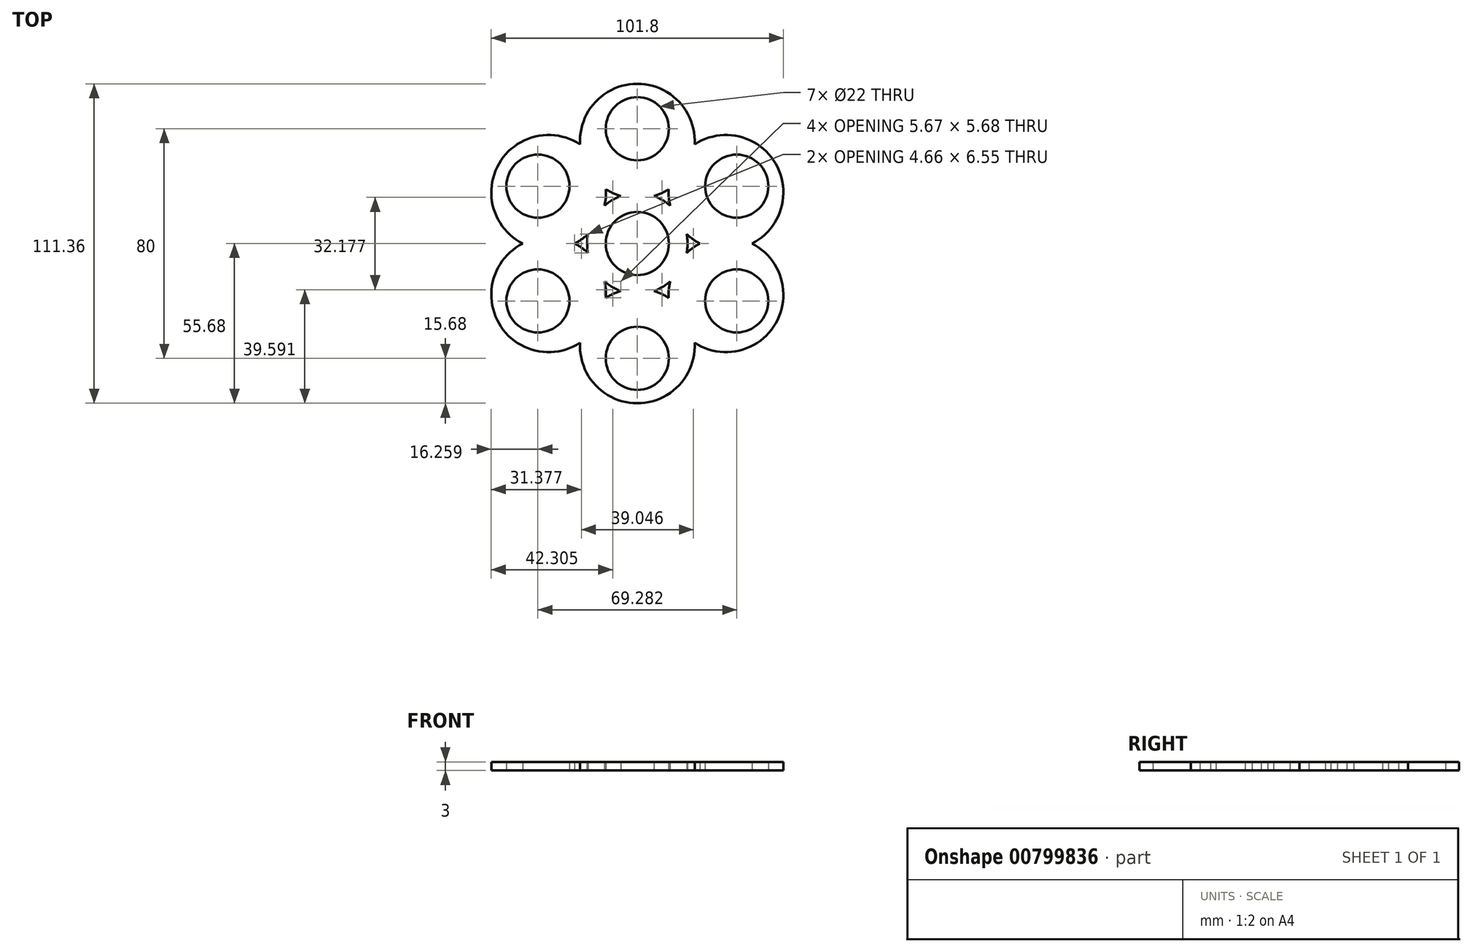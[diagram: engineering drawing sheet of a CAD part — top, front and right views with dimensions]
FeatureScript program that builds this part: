
annotation { "Feature Type Name" : "Feature", "Feature Type Description" : "" }
export const myFeature = defineFeature(function(context is Context, id is Id, definition is map)
    precondition{}
    {
        {
            var Q0;
            Q0=qCreatedBy(makeId("Top.planeOp"),FACE);
            var sketch = newSketch(context, id + "F0", { "sketchPlane" : qUnion([Q0])});
            skArc(sketch, "E0", {"start": v(5.5, 9.53) * mm, "mid": v(0, 11) * mm, "end": v(-5.5, 9.53) * mm});
            skArc(sketch, "E1", {"start": v(-5.76, 16.53) * mm, "mid": v(-7.29, 15.91) * mm, "end": v(-8.75, 15.16) * mm});
            skCircle(sketch, "E2", {"center": v(0, 40) * mm, "radius": 11 * mm});
            skArc(sketch, "E3", {"start": v(-10.93, 18.93) * mm, "mid": v(-8.43, 17.54) * mm, "end": v(-5.76, 16.53) * mm});
            skArc(sketch, "E4.trimOffspring", {"start": v(5.76, 16.53) * mm, "mid": v(8.43, 17.54) * mm, "end": v(10.93, 18.93) * mm});
            skArc(sketch, "E5.trimOffspring", {"start": v(19.97, 34.59) * mm, "mid": v(0, 55.68) * mm, "end": v(-19.97, 34.59) * mm});
            skArc(sketch, "E6.trimOffspring", {"start": v(8.75, 15.16) * mm, "mid": v(7.29, 15.91) * mm, "end": v(5.76, 16.53) * mm});
            skCircle(sketch, "E7.1.0", {"center": v(-34.64, 20) * mm, "radius": 11 * mm});
            skArc(sketch, "E7.1.1", {"start": v(-19.97, 34.59) * mm, "mid": v(-48.22, 27.84) * mm, "end": v(-39.94, 0) * mm});
            skArc(sketch, "E7.1.2", {"start": v(-5.5, 9.53) * mm, "mid": v(-9.53, 5.5) * mm, "end": v(-11, 0) * mm});
            skArc(sketch, "E7.1.3", {"start": v(-11.43, 13.25) * mm, "mid": v(-10.98, 16.07) * mm, "end": v(-10.93, 18.93) * mm});
            skArc(sketch, "E7.1.4", {"start": v(-21.86, 0) * mm, "mid": v(-19.4, 1.47) * mm, "end": v(-17.2, 3.27) * mm});
            skArc(sketch, "E7.1.5", {"start": v(-17.2, 3.27) * mm, "mid": v(-17.42, 1.64) * mm, "end": v(-17.5, 0) * mm});
            skArc(sketch, "E7.1.6", {"start": v(-8.75, 15.16) * mm, "mid": v(-10.14, 14.27) * mm, "end": v(-11.43, 13.25) * mm});
            skCircle(sketch, "E7.2.0", {"center": v(-34.64, -20) * mm, "radius": 11 * mm});
            skArc(sketch, "E7.2.1", {"start": v(-39.94, 0) * mm, "mid": v(-48.22, -27.84) * mm, "end": v(-19.97, -34.59) * mm});
            skArc(sketch, "E7.2.2", {"start": v(-11, 0) * mm, "mid": v(-9.53, -5.5) * mm, "end": v(-5.5, -9.53) * mm});
            skArc(sketch, "E7.2.3", {"start": v(-17.2, -3.27) * mm, "mid": v(-19.4, -1.47) * mm, "end": v(-21.86, 0) * mm});
            skArc(sketch, "E7.2.4", {"start": v(-10.93, -18.93) * mm, "mid": v(-10.98, -16.07) * mm, "end": v(-11.43, -13.25) * mm});
            skArc(sketch, "E7.2.5", {"start": v(-11.43, -13.25) * mm, "mid": v(-10.14, -14.27) * mm, "end": v(-8.75, -15.16) * mm});
            skArc(sketch, "E7.2.6", {"start": v(-17.5, 0) * mm, "mid": v(-17.42, -1.64) * mm, "end": v(-17.2, -3.27) * mm});
            skCircle(sketch, "E7.3.0", {"center": v(0, -40) * mm, "radius": 11 * mm});
            skArc(sketch, "E7.3.1", {"start": v(-19.97, -34.59) * mm, "mid": v(0, -55.68) * mm, "end": v(19.97, -34.59) * mm});
            skArc(sketch, "E7.3.2", {"start": v(-5.5, -9.53) * mm, "mid": v(0, -11) * mm, "end": v(5.5, -9.53) * mm});
            skArc(sketch, "E7.3.3", {"start": v(-5.76, -16.53) * mm, "mid": v(-8.43, -17.54) * mm, "end": v(-10.93, -18.93) * mm});
            skArc(sketch, "E7.3.4", {"start": v(10.93, -18.93) * mm, "mid": v(8.43, -17.54) * mm, "end": v(5.76, -16.53) * mm});
            skArc(sketch, "E7.3.5", {"start": v(5.76, -16.53) * mm, "mid": v(7.29, -15.91) * mm, "end": v(8.75, -15.16) * mm});
            skArc(sketch, "E7.3.6", {"start": v(-8.75, -15.16) * mm, "mid": v(-7.29, -15.91) * mm, "end": v(-5.76, -16.53) * mm});
            skCircle(sketch, "E7.4.0", {"center": v(34.64, -20) * mm, "radius": 11 * mm});
            skArc(sketch, "E7.4.1", {"start": v(19.97, -34.59) * mm, "mid": v(48.22, -27.84) * mm, "end": v(39.94, 0) * mm});
            skArc(sketch, "E7.4.2", {"start": v(5.5, -9.53) * mm, "mid": v(9.53, -5.5) * mm, "end": v(11, 0) * mm});
            skArc(sketch, "E7.4.3", {"start": v(11.43, -13.25) * mm, "mid": v(10.98, -16.07) * mm, "end": v(10.93, -18.93) * mm});
            skArc(sketch, "E7.4.4", {"start": v(21.86, 0) * mm, "mid": v(19.4, -1.47) * mm, "end": v(17.2, -3.27) * mm});
            skArc(sketch, "E7.4.5", {"start": v(17.2, -3.27) * mm, "mid": v(17.42, -1.64) * mm, "end": v(17.5, 0) * mm});
            skArc(sketch, "E7.4.6", {"start": v(8.75, -15.16) * mm, "mid": v(10.14, -14.27) * mm, "end": v(11.43, -13.25) * mm});
            skCircle(sketch, "E7.5.0", {"center": v(34.64, 20) * mm, "radius": 11 * mm});
            skArc(sketch, "E7.5.1", {"start": v(39.94, 0) * mm, "mid": v(48.22, 27.84) * mm, "end": v(19.97, 34.59) * mm});
            skArc(sketch, "E7.5.2", {"start": v(11, 0) * mm, "mid": v(9.53, 5.5) * mm, "end": v(5.5, 9.53) * mm});
            skArc(sketch, "E7.5.3", {"start": v(17.2, 3.27) * mm, "mid": v(19.4, 1.47) * mm, "end": v(21.86, 0) * mm});
            skArc(sketch, "E7.5.4", {"start": v(10.93, 18.93) * mm, "mid": v(10.98, 16.07) * mm, "end": v(11.43, 13.25) * mm});
            skArc(sketch, "E7.5.5", {"start": v(11.43, 13.25) * mm, "mid": v(10.14, 14.27) * mm, "end": v(8.75, 15.16) * mm});
            skArc(sketch, "E7.5.6", {"start": v(17.5, 0) * mm, "mid": v(17.42, 1.64) * mm, "end": v(17.2, 3.27) * mm});
            skSolve(sketch);
        }
        {
            var Q0;
            Q0 = qSketchRegion(id + "F0", true);
            extrude(context, id + "F1", {"entities" : qUnion([Q0]), "depth" : 3 * mm, "offsetDistance" : 25 * mm});
        }
    });
